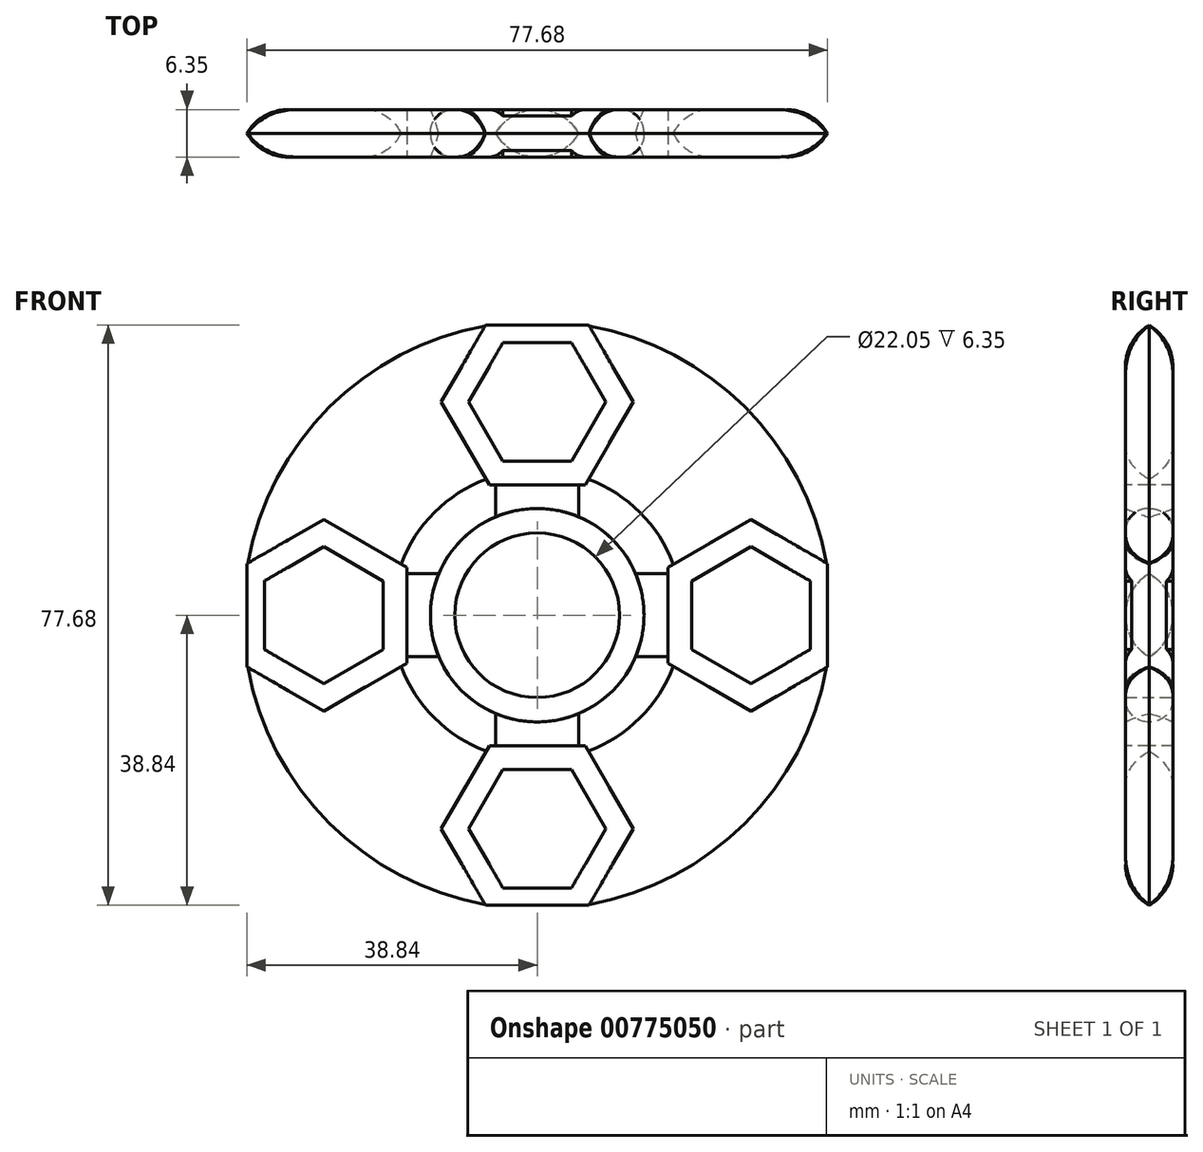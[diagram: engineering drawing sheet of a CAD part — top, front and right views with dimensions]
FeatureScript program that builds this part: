
annotation { "Feature Type Name" : "Feature", "Feature Type Description" : "" }
export const myFeature = defineFeature(function(context is Context, id is Id, definition is map)
    precondition{}
    {
        {
            var Q0;
            Q0=qCreatedBy(makeId("Front.planeOp"),FACE);
            var sketch = newSketch(context, id + "F0", { "sketchPlane" : qUnion([Q0])});
            skCircle(sketch, "E0", {"center": v(0, 0) * mm, "radius": 11.02 * mm});
            skCircle(sketch, "E1", {"center": v(0, 0) * mm, "radius": 14.29 * mm});
            skCircle(sketch, "E2.cCircle", {"center": v(0, 28.58) * mm, "radius": 7.94 * mm, "construction": true});
            skLineSegment(sketch, "E2.0", {"start": v(4.58, 20.64) * mm, "end": v(-4.58, 20.64) * mm});
            skLineSegment(sketch, "E2.1", {"start": v(-4.58, 20.64) * mm, "end": v(-9.17, 28.57) * mm});
            skLineSegment(sketch, "E2.2", {"start": v(-9.17, 28.57) * mm, "end": v(-4.58, 36.51) * mm});
            skLineSegment(sketch, "E2.3", {"start": v(-4.58, 36.51) * mm, "end": v(4.58, 36.51) * mm});
            skLineSegment(sketch, "E2.4", {"start": v(4.58, 36.51) * mm, "end": v(9.17, 28.58) * mm});
            skLineSegment(sketch, "E2.5", {"start": v(9.17, 28.57) * mm, "end": v(4.58, 20.64) * mm});
            skPoint(sketch, "E2.0.midPoint", {"position": v(0, 20.64) * mm});
            skCircle(sketch, "E3.cCircle", {"center": v(0, 28.58) * mm, "radius": 11.11 * mm, "construction": true});
            skLineSegment(sketch, "E3.0", {"start": v(6.42, 17.46) * mm, "end": v(-6.42, 17.46) * mm});
            skLineSegment(sketch, "E3.1", {"start": v(-6.42, 17.46) * mm, "end": v(-12.83, 28.57) * mm});
            skLineSegment(sketch, "E3.2", {"start": v(-12.83, 28.57) * mm, "end": v(-6.42, 39.69) * mm});
            skLineSegment(sketch, "E3.3", {"start": v(-6.42, 39.69) * mm, "end": v(6.42, 39.69) * mm});
            skLineSegment(sketch, "E3.4", {"start": v(6.42, 39.69) * mm, "end": v(12.83, 28.57) * mm});
            skLineSegment(sketch, "E3.5", {"start": v(12.83, 28.58) * mm, "end": v(6.42, 17.46) * mm});
            skPoint(sketch, "E3.0.midPoint", {"position": v(0, 17.46) * mm});
            skCircle(sketch, "E4.1.0", {"center": v(-28.58, 0) * mm, "radius": 7.94 * mm, "construction": true});
            skLineSegment(sketch, "E4.1.1", {"start": v(-20.64, 4.58) * mm, "end": v(-20.64, -4.58) * mm});
            skLineSegment(sketch, "E4.1.2", {"start": v(-28.57, -9.17) * mm, "end": v(-36.51, -4.58) * mm});
            skLineSegment(sketch, "E4.1.3", {"start": v(-28.58, 12.83) * mm, "end": v(-17.46, 6.42) * mm});
            skLineSegment(sketch, "E4.1.4", {"start": v(-39.69, 6.42) * mm, "end": v(-28.57, 12.83) * mm});
            skLineSegment(sketch, "E4.1.5", {"start": v(-39.69, -6.42) * mm, "end": v(-39.69, 6.42) * mm});
            skLineSegment(sketch, "E4.1.6", {"start": v(-20.64, -4.58) * mm, "end": v(-28.57, -9.17) * mm});
            skLineSegment(sketch, "E4.1.7", {"start": v(-36.51, -4.58) * mm, "end": v(-36.51, 4.58) * mm});
            skLineSegment(sketch, "E4.1.8", {"start": v(-36.51, 4.58) * mm, "end": v(-28.58, 9.17) * mm});
            skLineSegment(sketch, "E4.1.9", {"start": v(-28.57, 9.17) * mm, "end": v(-20.64, 4.58) * mm});
            skCircle(sketch, "E4.1.10", {"center": v(-28.58, 0) * mm, "radius": 11.11 * mm, "construction": true});
            skLineSegment(sketch, "E4.1.11", {"start": v(-17.46, 6.42) * mm, "end": v(-17.46, -6.42) * mm});
            skLineSegment(sketch, "E4.1.12", {"start": v(-28.57, -12.83) * mm, "end": v(-39.69, -6.42) * mm});
            skPoint(sketch, "E4.1.13", {"position": v(-20.64, 0) * mm});
            skLineSegment(sketch, "E4.1.14", {"start": v(-17.46, -6.42) * mm, "end": v(-28.57, -12.83) * mm});
            skCircle(sketch, "E4.2.0", {"center": v(0, -28.58) * mm, "radius": 7.94 * mm, "construction": true});
            skLineSegment(sketch, "E4.2.1", {"start": v(-4.58, -20.64) * mm, "end": v(4.58, -20.64) * mm});
            skLineSegment(sketch, "E4.2.2", {"start": v(9.17, -28.57) * mm, "end": v(4.58, -36.51) * mm});
            skLineSegment(sketch, "E4.2.3", {"start": v(-12.83, -28.58) * mm, "end": v(-6.42, -17.46) * mm});
            skLineSegment(sketch, "E4.2.4", {"start": v(-6.42, -39.69) * mm, "end": v(-12.83, -28.57) * mm});
            skLineSegment(sketch, "E4.2.5", {"start": v(6.42, -39.69) * mm, "end": v(-6.42, -39.69) * mm});
            skLineSegment(sketch, "E4.2.6", {"start": v(4.58, -20.64) * mm, "end": v(9.17, -28.57) * mm});
            skLineSegment(sketch, "E4.2.7", {"start": v(4.58, -36.51) * mm, "end": v(-4.58, -36.51) * mm});
            skLineSegment(sketch, "E4.2.8", {"start": v(-4.58, -36.51) * mm, "end": v(-9.17, -28.58) * mm});
            skLineSegment(sketch, "E4.2.9", {"start": v(-9.17, -28.57) * mm, "end": v(-4.58, -20.64) * mm});
            skCircle(sketch, "E4.2.10", {"center": v(0, -28.58) * mm, "radius": 11.11 * mm, "construction": true});
            skLineSegment(sketch, "E4.2.11", {"start": v(-6.42, -17.46) * mm, "end": v(6.42, -17.46) * mm});
            skLineSegment(sketch, "E4.2.12", {"start": v(12.83, -28.57) * mm, "end": v(6.42, -39.69) * mm});
            skPoint(sketch, "E4.2.13", {"position": v(0, -20.64) * mm});
            skLineSegment(sketch, "E4.2.14", {"start": v(6.42, -17.46) * mm, "end": v(12.83, -28.57) * mm});
            skCircle(sketch, "E4.3.0", {"center": v(28.58, 0) * mm, "radius": 7.94 * mm, "construction": true});
            skLineSegment(sketch, "E4.3.1", {"start": v(20.64, -4.58) * mm, "end": v(20.64, 4.58) * mm});
            skLineSegment(sketch, "E4.3.2", {"start": v(28.57, 9.17) * mm, "end": v(36.51, 4.58) * mm});
            skLineSegment(sketch, "E4.3.3", {"start": v(28.57, -12.83) * mm, "end": v(17.46, -6.42) * mm});
            skLineSegment(sketch, "E4.3.4", {"start": v(39.69, -6.42) * mm, "end": v(28.57, -12.83) * mm});
            skLineSegment(sketch, "E4.3.5", {"start": v(39.69, 6.42) * mm, "end": v(39.69, -6.42) * mm});
            skLineSegment(sketch, "E4.3.6", {"start": v(20.64, 4.58) * mm, "end": v(28.57, 9.17) * mm});
            skLineSegment(sketch, "E4.3.7", {"start": v(36.51, 4.58) * mm, "end": v(36.51, -4.58) * mm});
            skLineSegment(sketch, "E4.3.8", {"start": v(36.51, -4.58) * mm, "end": v(28.58, -9.17) * mm});
            skLineSegment(sketch, "E4.3.9", {"start": v(28.57, -9.17) * mm, "end": v(20.64, -4.58) * mm});
            skCircle(sketch, "E4.3.10", {"center": v(28.58, 0) * mm, "radius": 11.11 * mm, "construction": true});
            skLineSegment(sketch, "E4.3.11", {"start": v(17.46, -6.42) * mm, "end": v(17.46, 6.42) * mm});
            skLineSegment(sketch, "E4.3.12", {"start": v(28.57, 12.83) * mm, "end": v(39.69, 6.42) * mm});
            skPoint(sketch, "E4.3.13", {"position": v(20.64, 0) * mm});
            skLineSegment(sketch, "E4.3.14", {"start": v(17.46, 6.42) * mm, "end": v(28.57, 12.83) * mm});
            skSolve(sketch);
        }
        {
            var Q0;
            Q0=qCreatedBy(makeId("Front.planeOp"),FACE);
            var sketch = newSketch(context, id + "F1", { "sketchPlane" : qUnion([Q0])});
            skCircle(sketch, "E5.0", {"center": v(0, 28.58) * mm, "radius": 7.94 * mm});
            skLineSegment(sketch, "E5.1", {"start": v(4.58, 20.64) * mm, "end": v(-4.58, 20.64) * mm});
            skLineSegment(sketch, "E5.2", {"start": v(-4.58, 20.64) * mm, "end": v(-9.17, 28.57) * mm});
            skLineSegment(sketch, "E5.3", {"start": v(-9.17, 28.57) * mm, "end": v(-4.58, 36.51) * mm});
            skLineSegment(sketch, "E5.4", {"start": v(12.83, -28.57) * mm, "end": v(6.42, -39.69) * mm});
            skCircle(sketch, "E5.5", {"center": v(-28.58, 0) * mm, "radius": 11.11 * mm});
            skCircle(sketch, "E5.6", {"center": v(0, 0) * mm, "radius": 14.29 * mm});
            skCircle(sketch, "E5.7", {"center": v(0, 0) * mm, "radius": 11.02 * mm});
            skLineSegment(sketch, "E5.8", {"start": v(12.83, 28.58) * mm, "end": v(6.42, 17.46) * mm});
            skLineSegment(sketch, "E5.9", {"start": v(6.42, 39.69) * mm, "end": v(12.83, 28.57) * mm});
            skLineSegment(sketch, "E5.10", {"start": v(-6.42, 39.69) * mm, "end": v(6.42, 39.69) * mm});
            skLineSegment(sketch, "E5.11", {"start": v(6.42, -39.69) * mm, "end": v(-6.42, -39.69) * mm});
            skLineSegment(sketch, "E5.12", {"start": v(36.51, 4.58) * mm, "end": v(36.51, -4.58) * mm});
            skLineSegment(sketch, "E5.13", {"start": v(-28.58, 12.83) * mm, "end": v(-17.46, 6.42) * mm});
            skLineSegment(sketch, "E5.14", {"start": v(-4.58, 36.51) * mm, "end": v(4.58, 36.51) * mm});
            skLineSegment(sketch, "E5.15", {"start": v(4.58, 36.51) * mm, "end": v(9.17, 28.58) * mm});
            skLineSegment(sketch, "E5.16", {"start": v(9.17, 28.57) * mm, "end": v(4.58, 20.64) * mm});
            skCircle(sketch, "E5.17", {"center": v(0, 28.58) * mm, "radius": 11.11 * mm});
            skLineSegment(sketch, "E5.18", {"start": v(6.42, 17.46) * mm, "end": v(-6.42, 17.46) * mm});
            skLineSegment(sketch, "E5.19", {"start": v(-6.42, 17.46) * mm, "end": v(-12.83, 28.57) * mm});
            skLineSegment(sketch, "E5.20", {"start": v(-12.83, 28.57) * mm, "end": v(-6.42, 39.69) * mm});
            skLineSegment(sketch, "E5.21", {"start": v(6.42, -17.46) * mm, "end": v(12.83, -28.57) * mm});
            skLineSegment(sketch, "E5.22", {"start": v(-17.46, 6.42) * mm, "end": v(-17.46, -6.42) * mm});
            skLineSegment(sketch, "E5.23", {"start": v(17.46, -6.42) * mm, "end": v(17.46, 6.42) * mm});
            skLineSegment(sketch, "E5.24", {"start": v(-9.17, -28.57) * mm, "end": v(-4.58, -20.64) * mm});
            skLineSegment(sketch, "E5.25", {"start": v(-36.51, -4.58) * mm, "end": v(-36.51, 4.58) * mm});
            skLineSegment(sketch, "E5.26", {"start": v(-39.69, 6.42) * mm, "end": v(-28.57, 12.83) * mm});
            skLineSegment(sketch, "E5.27", {"start": v(36.51, -4.58) * mm, "end": v(28.58, -9.17) * mm});
            skLineSegment(sketch, "E5.28", {"start": v(20.64, -4.58) * mm, "end": v(20.64, 4.58) * mm});
            skLineSegment(sketch, "E5.29", {"start": v(4.58, -20.64) * mm, "end": v(9.17, -28.57) * mm});
            skLineSegment(sketch, "E5.30", {"start": v(-17.46, -6.42) * mm, "end": v(-28.57, -12.83) * mm});
            skCircle(sketch, "E5.31", {"center": v(-28.58, 0) * mm, "radius": 7.94 * mm});
            skLineSegment(sketch, "E5.32", {"start": v(39.69, -6.42) * mm, "end": v(28.57, -12.83) * mm});
            skLineSegment(sketch, "E5.33", {"start": v(9.17, -28.57) * mm, "end": v(4.58, -36.51) * mm});
            skCircle(sketch, "E5.34", {"center": v(28.58, 0) * mm, "radius": 7.94 * mm});
            skLineSegment(sketch, "E5.35", {"start": v(-28.57, -12.83) * mm, "end": v(-39.69, -6.42) * mm});
            skLineSegment(sketch, "E5.36", {"start": v(28.57, 12.83) * mm, "end": v(39.69, 6.42) * mm});
            skCircle(sketch, "E5.37", {"center": v(0, -28.58) * mm, "radius": 11.11 * mm});
            skLineSegment(sketch, "E5.38", {"start": v(-36.51, 4.58) * mm, "end": v(-28.58, 9.17) * mm});
            skLineSegment(sketch, "E5.39", {"start": v(-39.69, -6.42) * mm, "end": v(-39.69, 6.42) * mm});
            skLineSegment(sketch, "E5.40", {"start": v(28.57, 9.17) * mm, "end": v(36.51, 4.58) * mm});
            skLineSegment(sketch, "E5.41", {"start": v(28.57, -9.17) * mm, "end": v(20.64, -4.58) * mm});
            skLineSegment(sketch, "E5.42", {"start": v(4.58, -36.51) * mm, "end": v(-4.58, -36.51) * mm});
            skCircle(sketch, "E5.43", {"center": v(0, -28.58) * mm, "radius": 7.94 * mm});
            skLineSegment(sketch, "E5.44", {"start": v(-20.64, 4.58) * mm, "end": v(-20.64, -4.58) * mm});
            skLineSegment(sketch, "E5.45", {"start": v(39.69, 6.42) * mm, "end": v(39.69, -6.42) * mm});
            skLineSegment(sketch, "E5.46", {"start": v(-12.83, -28.58) * mm, "end": v(-6.42, -17.46) * mm});
            skLineSegment(sketch, "E5.47", {"start": v(17.46, 6.42) * mm, "end": v(28.57, 12.83) * mm});
            skLineSegment(sketch, "E5.48", {"start": v(-6.42, -17.46) * mm, "end": v(6.42, -17.46) * mm});
            skLineSegment(sketch, "E5.49", {"start": v(-28.57, 9.17) * mm, "end": v(-20.64, 4.58) * mm});
            skLineSegment(sketch, "E5.50", {"start": v(-20.64, -4.58) * mm, "end": v(-28.57, -9.17) * mm});
            skCircle(sketch, "E5.51", {"center": v(28.58, 0) * mm, "radius": 11.11 * mm});
            skLineSegment(sketch, "E5.52", {"start": v(28.57, -12.83) * mm, "end": v(17.46, -6.42) * mm});
            skLineSegment(sketch, "E5.53", {"start": v(-4.58, -36.51) * mm, "end": v(-9.17, -28.58) * mm});
            skLineSegment(sketch, "E5.54", {"start": v(-4.58, -20.64) * mm, "end": v(4.58, -20.64) * mm});
            skLineSegment(sketch, "E5.55", {"start": v(-28.57, -9.17) * mm, "end": v(-36.51, -4.58) * mm});
            skLineSegment(sketch, "E5.56", {"start": v(20.64, 4.58) * mm, "end": v(28.57, 9.17) * mm});
            skLineSegment(sketch, "E5.57", {"start": v(-6.42, -39.69) * mm, "end": v(-12.83, -28.57) * mm});
            skCircle(sketch, "E6", {"center": v(0, 0) * mm, "radius": 40.2 * mm});
            skArc(sketch, "E7", {"start": v(-17.46, -6.42) * mm, "mid": v(-13.15, -13.15) * mm, "end": v(-6.42, -17.46) * mm});
            skArc(sketch, "E8.trimOffspring", {"start": v(6.42, -17.46) * mm, "mid": v(13.15, -13.15) * mm, "end": v(17.46, -6.42) * mm});
            skArc(sketch, "E9.trimOffspring", {"start": v(17.46, 6.42) * mm, "mid": v(13.15, 13.15) * mm, "end": v(6.42, 17.46) * mm});
            skArc(sketch, "E10.trimOffspring", {"start": v(-6.42, 17.46) * mm, "mid": v(-13.15, 13.15) * mm, "end": v(-17.46, 6.42) * mm});
            skLineSegment(sketch, "E11", {"start": v(-17.46, 6.42) * mm, "end": v(-12.77, 6.42) * mm});
            skLineSegment(sketch, "E12", {"start": v(-17.46, -6.42) * mm, "end": v(-12.77, -6.42) * mm});
            skLineSegment(sketch, "E13", {"start": v(-6.42, -17.46) * mm, "end": v(-6.42, -12.77) * mm});
            skLineSegment(sketch, "E14", {"start": v(6.42, -17.46) * mm, "end": v(6.42, -12.77) * mm});
            skLineSegment(sketch, "E15", {"start": v(17.46, -6.42) * mm, "end": v(12.77, -6.42) * mm});
            skLineSegment(sketch, "E16", {"start": v(17.46, 6.42) * mm, "end": v(12.77, 6.42) * mm});
            skLineSegment(sketch, "E17", {"start": v(6.42, 17.46) * mm, "end": v(6.42, 12.77) * mm});
            skLineSegment(sketch, "E18", {"start": v(-6.42, 17.46) * mm, "end": v(-6.42, 12.77) * mm});
            skSolve(sketch);
        }
        {
            var Q0;
            Q0 = qSketchRegion(id + "F0", true);
            var Q1;
            {var subQ9=sQuery(id+"F1.wireOp",EDGE,"E10.trimOffspring");Q1=makeQuery(id+"F1.imprint","IMPRINT",FACE,{"disambiguationData":[TD([[makeQuery(id+"F1.imprint","IMPRINT",EDGE,{"derivedFrom":subQ9}),-1.0]])]});}
            var Q2;
            {var subQ13=sQuery(id+"F1.wireOp",EDGE,"E9.trimOffspring");Q2=makeQuery(id+"F1.imprint","IMPRINT",FACE,{"disambiguationData":[TD([[makeQuery(id+"F1.imprint","IMPRINT",EDGE,{"derivedFrom":subQ13}),-1.0]])]});}
            var Q3;
            {var subQ9=sQuery(id+"F1.wireOp",EDGE,"E8.trimOffspring");Q3=makeQuery(id+"F1.imprint","IMPRINT",FACE,{"disambiguationData":[TD([[makeQuery(id+"F1.imprint","IMPRINT",EDGE,{"derivedFrom":subQ9}),-1.0]])]});}
            var Q4;
            {var subQ11=sQuery(id+"F1.wireOp",EDGE,"E7");Q4=makeQuery(id+"F1.imprint","IMPRINT",FACE,{"disambiguationData":[TD([[makeQuery(id+"F1.imprint","IMPRINT",EDGE,{"derivedFrom":subQ11}),-1.0]])]});}
            var Q5;
            {var subQ0=sQuery(id+"F1.wireOp",EDGE,"E13");Q5=makeQuery(id+"F1.imprint","IMPRINT",FACE,{"disambiguationData":[TD([[makeQuery(id+"F1.imprint","IMPRINT",EDGE,{"derivedFrom":subQ0}),-1.0]])]});}
            var Q6;
            {var subQ0=sQuery(id+"F1.wireOp",EDGE,"E15");Q6=makeQuery(id+"F1.imprint","IMPRINT",FACE,{"disambiguationData":[TD([[makeQuery(id+"F1.imprint","IMPRINT",EDGE,{"derivedFrom":subQ0}),-1.0]])]});}
            var Q7;
            {var subQ3=sQuery(id+"F1.wireOp",EDGE,"E17");Q7=makeQuery(id+"F1.imprint","IMPRINT",FACE,{"disambiguationData":[TD([[makeQuery(id+"F1.imprint","IMPRINT",EDGE,{"derivedFrom":subQ3}),-1.0]])]});}
            var Q8;
            {var subQ0=sQuery(id+"F1.wireOp",EDGE,"E11");Q8=makeQuery(id+"F1.imprint","IMPRINT",FACE,{"disambiguationData":[TD([[makeQuery(id+"F1.imprint","IMPRINT",EDGE,{"derivedFrom":subQ0}),-1.0]])]});}
            extrude(context, id + "F2", {"entities" : qUnion([Q0, Q1, Q2, Q3, Q4, Q5, Q6, Q7, Q8]), "depth" : 6.35 * mm, "offsetDistance" : 25.4 * mm});
        }
        {
            var Q0;
            {var subQ0=sQuery(id+"F1.wireOp",EDGE,"E6");Q0=makeQuery(id+"F2.opExtrude","CAP_EDGE",EDGE,{"disambiguationData":[OSD([subQ0]),TDD([makeQuery(id+"F1.imprint","IMPRINT",EDGE,{"disambiguationData":[TD([[makeQuery(id+"F1.imprint","INTERSECT",VERTEX,{"derivedFrom":[sQuery(id+"F1.wireOp",EDGE,"E5.9"),sQuery(id+"F1.wireOp",EDGE,"E5.10"),subQ0]}),1.0]])],"derivedFrom":subQ0})])],"isStart":false});}
            var Q1;
            {var subQ0=sQuery(id+"F1.wireOp",EDGE,"E6");Q1=makeQuery(id+"F2.opExtrude","CAP_EDGE",EDGE,{"disambiguationData":[OSD([subQ0]),TDD([makeQuery(id+"F1.imprint","IMPRINT",EDGE,{"disambiguationData":[TD([[makeQuery(id+"F1.imprint","INTERSECT",VERTEX,{"derivedFrom":[sQuery(id+"F1.wireOp",EDGE,"E5.4"),sQuery(id+"F1.wireOp",EDGE,"E5.11"),subQ0]}),-1.0]])],"derivedFrom":subQ0})])],"isStart":false});}
            var Q2;
            {var subQ0=sQuery(id+"F1.wireOp",EDGE,"E6");Q2=makeQuery(id+"F2.opExtrude","CAP_EDGE",EDGE,{"disambiguationData":[OSD([subQ0]),TDD([makeQuery(id+"F1.imprint","IMPRINT",EDGE,{"disambiguationData":[TD([[makeQuery(id+"F1.imprint","INTERSECT",VERTEX,{"derivedFrom":[sQuery(id+"F1.wireOp",EDGE,"E5.11"),sQuery(id+"F1.wireOp",EDGE,"E5.57"),subQ0]}),1.0]])],"derivedFrom":subQ0})])],"isStart":false});}
            var Q3;
            {var subQ0=sQuery(id+"F1.wireOp",EDGE,"E6");Q3=makeQuery(id+"F2.opExtrude","CAP_EDGE",EDGE,{"disambiguationData":[OSD([subQ0]),TDD([makeQuery(id+"F1.imprint","IMPRINT",EDGE,{"disambiguationData":[TD([[makeQuery(id+"F1.imprint","INTERSECT",VERTEX,{"derivedFrom":[sQuery(id+"F1.wireOp",EDGE,"E5.10"),sQuery(id+"F1.wireOp",EDGE,"E5.20"),subQ0]}),-1.0]])],"derivedFrom":subQ0})])],"isStart":false});}
            var Q4;
            Q4=makeQuery(id+"F2.opExtrude","CAP_EDGE",EDGE,{"disambiguationData":[OSD([sQuery(id+"F0.wireOp",EDGE,"E3.3")])],"isStart":false});
            var Q5;
            Q5=makeQuery(id+"F2.opExtrude","CAP_EDGE",EDGE,{"disambiguationData":[OSD([sQuery(id+"F0.wireOp",EDGE,"E4.1.5")])],"isStart":false});
            var Q6;
            Q6=makeQuery(id+"F2.opExtrude","CAP_EDGE",EDGE,{"disambiguationData":[OSD([sQuery(id+"F0.wireOp",EDGE,"E4.3.5")])],"isStart":false});
            var Q7;
            Q7=makeQuery(id+"F2.opExtrude","CAP_EDGE",EDGE,{"disambiguationData":[OSD([sQuery(id+"F0.wireOp",EDGE,"E4.2.5")])],"isStart":false});
            var Q8;
            {var subQ0=sQuery(id+"F1.wireOp",EDGE,"E6");Q8=makeQuery(id+"F2.opExtrude","CAP_EDGE",EDGE,{"disambiguationData":[OSD([subQ0]),TDD([makeQuery(id+"F1.imprint","IMPRINT",EDGE,{"disambiguationData":[TD([[makeQuery(id+"F1.imprint","INTERSECT",VERTEX,{"derivedFrom":[sQuery(id+"F1.wireOp",EDGE,"E5.4"),sQuery(id+"F1.wireOp",EDGE,"E5.11"),subQ0]}),-1.0]])],"derivedFrom":subQ0})])],"isStart":true});}
            var Q9;
            Q9=makeQuery(id+"F2.opExtrude","CAP_EDGE",EDGE,{"disambiguationData":[OSD([sQuery(id+"F0.wireOp",EDGE,"E4.3.5")])],"isStart":true});
            var Q10;
            {var subQ0=sQuery(id+"F1.wireOp",EDGE,"E6");Q10=makeQuery(id+"F2.opExtrude","CAP_EDGE",EDGE,{"disambiguationData":[OSD([subQ0]),TDD([makeQuery(id+"F1.imprint","IMPRINT",EDGE,{"disambiguationData":[TD([[makeQuery(id+"F1.imprint","INTERSECT",VERTEX,{"derivedFrom":[sQuery(id+"F1.wireOp",EDGE,"E5.9"),sQuery(id+"F1.wireOp",EDGE,"E5.10"),subQ0]}),1.0]])],"derivedFrom":subQ0})])],"isStart":true});}
            var Q11;
            Q11=makeQuery(id+"F2.opExtrude","CAP_EDGE",EDGE,{"disambiguationData":[OSD([sQuery(id+"F0.wireOp",EDGE,"E3.3")])],"isStart":true});
            var Q12;
            {var subQ0=sQuery(id+"F1.wireOp",EDGE,"E6");Q12=makeQuery(id+"F2.opExtrude","CAP_EDGE",EDGE,{"disambiguationData":[OSD([subQ0]),TDD([makeQuery(id+"F1.imprint","IMPRINT",EDGE,{"disambiguationData":[TD([[makeQuery(id+"F1.imprint","INTERSECT",VERTEX,{"derivedFrom":[sQuery(id+"F1.wireOp",EDGE,"E5.10"),sQuery(id+"F1.wireOp",EDGE,"E5.20"),subQ0]}),-1.0]])],"derivedFrom":subQ0})])],"isStart":true});}
            var Q13;
            Q13=makeQuery(id+"F2.opExtrude","CAP_EDGE",EDGE,{"disambiguationData":[OSD([sQuery(id+"F0.wireOp",EDGE,"E4.1.5")])],"isStart":true});
            var Q14;
            {var subQ0=sQuery(id+"F1.wireOp",EDGE,"E6");Q14=makeQuery(id+"F2.opExtrude","CAP_EDGE",EDGE,{"disambiguationData":[OSD([subQ0]),TDD([makeQuery(id+"F1.imprint","IMPRINT",EDGE,{"disambiguationData":[TD([[makeQuery(id+"F1.imprint","INTERSECT",VERTEX,{"derivedFrom":[sQuery(id+"F1.wireOp",EDGE,"E5.11"),sQuery(id+"F1.wireOp",EDGE,"E5.57"),subQ0]}),1.0]])],"derivedFrom":subQ0})])],"isStart":true});}
            var Q15;
            Q15=makeQuery(id+"F2.opExtrude","CAP_EDGE",EDGE,{"disambiguationData":[OSD([sQuery(id+"F0.wireOp",EDGE,"E4.2.5")])],"isStart":true});
            fillet(context, id + "F3", {"entities" : qUnion([Q0, Q1, Q2, Q3, Q4, Q5, Q6, Q7, Q8, Q9, Q10, Q11, Q12, Q13, Q14, Q15]), "radius" : 6.35 * mm, "tangentPropagation" : true, "allowEdgeOverflow" : false});
        }
        {
            var Q0;
            Q0=makeQuery(id+"F2.opExtrude","CAP_EDGE",EDGE,{"disambiguationData":[OSD([sQuery(id+"F1.wireOp",EDGE,"E14")])],"isStart":false});
            var Q1;
            Q1=makeQuery(id+"F2.opExtrude","CAP_EDGE",EDGE,{"disambiguationData":[OSD([sQuery(id+"F1.wireOp",EDGE,"E13")])],"isStart":false});
            var Q2;
            Q2=makeQuery(id+"F2.opExtrude","CAP_EDGE",EDGE,{"disambiguationData":[OSD([sQuery(id+"F1.wireOp",EDGE,"E12")])],"isStart":false});
            var Q3;
            Q3=makeQuery(id+"F2.opExtrude","CAP_EDGE",EDGE,{"disambiguationData":[OSD([sQuery(id+"F1.wireOp",EDGE,"E11")])],"isStart":false});
            var Q4;
            Q4=makeQuery(id+"F2.opExtrude","CAP_EDGE",EDGE,{"disambiguationData":[OSD([sQuery(id+"F1.wireOp",EDGE,"E18")])],"isStart":false});
            var Q5;
            Q5=makeQuery(id+"F2.opExtrude","CAP_EDGE",EDGE,{"disambiguationData":[OSD([sQuery(id+"F1.wireOp",EDGE,"E17")])],"isStart":false});
            var Q6;
            Q6=makeQuery(id+"F2.opExtrude","CAP_EDGE",EDGE,{"disambiguationData":[OSD([sQuery(id+"F1.wireOp",EDGE,"E16")])],"isStart":false});
            var Q7;
            Q7=makeQuery(id+"F2.opExtrude","CAP_EDGE",EDGE,{"disambiguationData":[OSD([sQuery(id+"F1.wireOp",EDGE,"E15")])],"isStart":false});
            var Q8;
            Q8=makeQuery(id+"F2.opExtrude","CAP_EDGE",EDGE,{"disambiguationData":[OSD([sQuery(id+"F1.wireOp",EDGE,"E18")])],"isStart":true});
            var Q9;
            Q9=makeQuery(id+"F2.opExtrude","CAP_EDGE",EDGE,{"disambiguationData":[OSD([sQuery(id+"F1.wireOp",EDGE,"E17")])],"isStart":true});
            var Q10;
            Q10=makeQuery(id+"F2.opExtrude","CAP_EDGE",EDGE,{"disambiguationData":[OSD([sQuery(id+"F1.wireOp",EDGE,"E16")])],"isStart":true});
            var Q11;
            Q11=makeQuery(id+"F2.opExtrude","CAP_EDGE",EDGE,{"disambiguationData":[OSD([sQuery(id+"F1.wireOp",EDGE,"E15")])],"isStart":true});
            var Q12;
            Q12=makeQuery(id+"F2.opExtrude","CAP_EDGE",EDGE,{"disambiguationData":[OSD([sQuery(id+"F1.wireOp",EDGE,"E14")])],"isStart":true});
            var Q13;
            Q13=makeQuery(id+"F2.opExtrude","CAP_EDGE",EDGE,{"disambiguationData":[OSD([sQuery(id+"F1.wireOp",EDGE,"E13")])],"isStart":true});
            var Q14;
            Q14=makeQuery(id+"F2.opExtrude","CAP_EDGE",EDGE,{"disambiguationData":[OSD([sQuery(id+"F1.wireOp",EDGE,"E12")])],"isStart":true});
            var Q15;
            Q15=makeQuery(id+"F2.opExtrude","CAP_EDGE",EDGE,{"disambiguationData":[OSD([sQuery(id+"F1.wireOp",EDGE,"E11")])],"isStart":true});
            fillet(context, id + "F4", {"entities" : qUnion([Q0, Q1, Q2, Q3, Q4, Q5, Q6, Q7, Q8, Q9, Q10, Q11, Q12, Q13, Q14, Q15]), "radius" : 6.35 * mm, "tangentPropagation" : true, "allowEdgeOverflow" : false});
        }
        {
            var Q0;
            Q0=makeQuery(id+"F2.opExtrude","CAP_EDGE",EDGE,{"disambiguationData":[OSD([sQuery(id+"F1.wireOp",EDGE,"E10.trimOffspring")])],"isStart":false});
            var Q1;
            Q1=makeQuery(id+"F2.opExtrude","CAP_EDGE",EDGE,{"disambiguationData":[OSD([sQuery(id+"F1.wireOp",EDGE,"E7")])],"isStart":false});
            var Q2;
            Q2=makeQuery(id+"F2.opExtrude","CAP_EDGE",EDGE,{"disambiguationData":[OSD([sQuery(id+"F1.wireOp",EDGE,"E8.trimOffspring")])],"isStart":false});
            var Q3;
            Q3=makeQuery(id+"F2.opExtrude","CAP_EDGE",EDGE,{"disambiguationData":[OSD([sQuery(id+"F1.wireOp",EDGE,"E9.trimOffspring")])],"isStart":false});
            var Q4;
            Q4=makeQuery(id+"F2.opExtrude","CAP_EDGE",EDGE,{"disambiguationData":[OSD([sQuery(id+"F1.wireOp",EDGE,"E8.trimOffspring")])],"isStart":true});
            var Q5;
            Q5=makeQuery(id+"F2.opExtrude","CAP_EDGE",EDGE,{"disambiguationData":[OSD([sQuery(id+"F1.wireOp",EDGE,"E7")])],"isStart":true});
            var Q6;
            Q6=makeQuery(id+"F2.opExtrude","CAP_EDGE",EDGE,{"disambiguationData":[OSD([sQuery(id+"F1.wireOp",EDGE,"E10.trimOffspring")])],"isStart":true});
            var Q7;
            Q7=makeQuery(id+"F2.opExtrude","CAP_EDGE",EDGE,{"disambiguationData":[OSD([sQuery(id+"F1.wireOp",EDGE,"E9.trimOffspring")])],"isStart":true});
            fillet(context, id + "F5", {"entities" : qUnion([Q0, Q1, Q2, Q3, Q4, Q5, Q6, Q7]), "radius" : 6.35 * mm, "tangentPropagation" : true, "allowEdgeOverflow" : false});
        }
        {
            var Q0;
            Q0=makeQuery(id+"F2.opExtrude","CAP_EDGE",EDGE,{"disambiguationData":[OSD([sQuery(id+"F0.wireOp",EDGE,"E1")])],"isStart":true});
            var Q1;
            Q1=makeQuery(id+"F2.opExtrude","CAP_EDGE",EDGE,{"disambiguationData":[OSD([sQuery(id+"F0.wireOp",EDGE,"E1")])],"isStart":false});
            fillet(context, id + "F6", {"entities" : qUnion([Q0, Q1]), "radius" : 3.05 * mm, "tangentPropagation" : true, "allowEdgeOverflow" : false});
        }
    });
